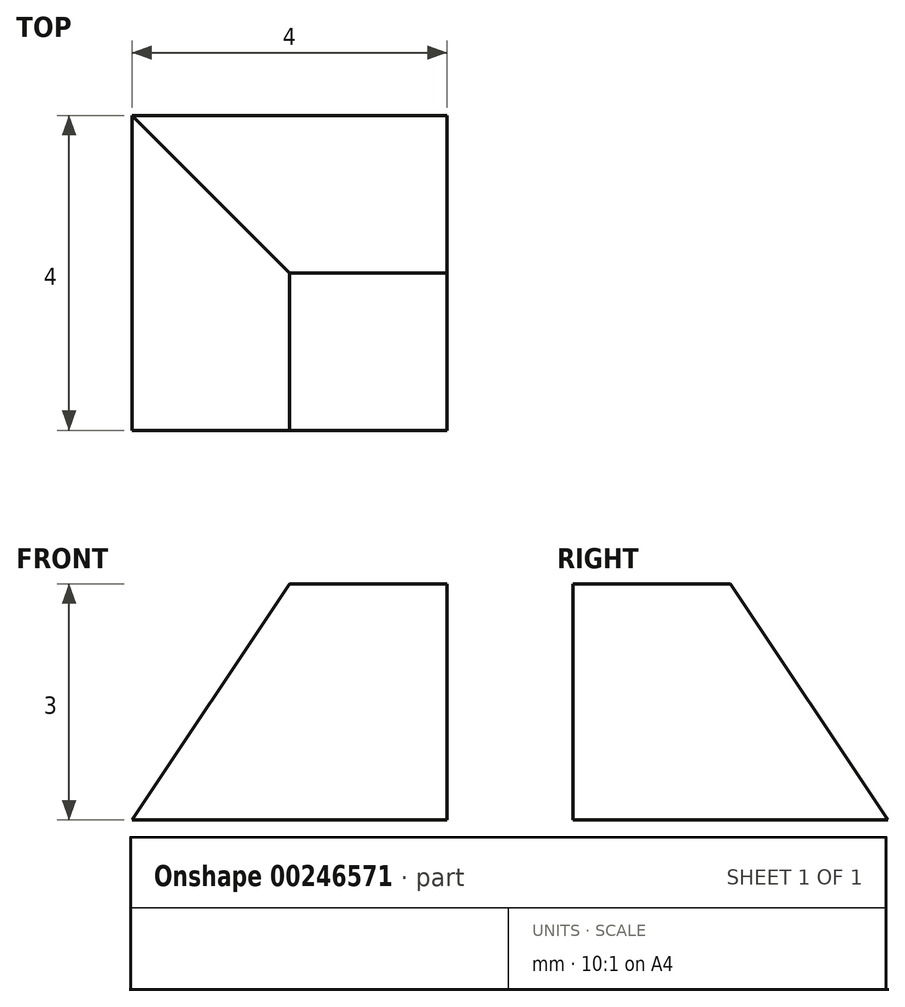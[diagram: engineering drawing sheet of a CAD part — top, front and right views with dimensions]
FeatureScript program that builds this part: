
annotation { "Feature Type Name" : "Feature", "Feature Type Description" : "" }
export const myFeature = defineFeature(function(context is Context, id is Id, definition is map)
    precondition{}
    {
        {
            var Q0;
            Q0=qCreatedBy(makeId("Top.planeOp"),FACE);
            var sketch = newSketch(context, id + "F0", { "sketchPlane" : qUnion([Q0])});
            skLineSegment(sketch, "E0.bottom", {"start": v(0, 0) * mm, "end": v(4, 0) * mm});
            skLineSegment(sketch, "E0.top", {"start": v(0, 4) * mm, "end": v(4, 4) * mm});
            skLineSegment(sketch, "E0.left", {"start": v(0, 0) * mm, "end": v(0, 4) * mm});
            skLineSegment(sketch, "E0.right", {"start": v(4, 0) * mm, "end": v(4, 4) * mm});
            skSolve(sketch);
        }
        {
            var Q0;
            Q0=makeQuery(id+"F0.imprint","IMPRINT",FACE,{"disambiguationData":[TD([[makeQuery(id+"F0.imprint","IMPRINT",EDGE,{"derivedFrom":sQuery(id+"F0.wireOp",EDGE,"E0.bottom")}),1.0]])]});
            extrude(context, id + "F1", {"entities" : qUnion([Q0]), "depth" : 3 * mm});
        }
        {
            var Q0;
            Q0=makeQuery(id+"F1.opExtrude","SWEPT_FACE",FACE,{"disambiguationData":[OSD([sQuery(id+"F0.wireOp",EDGE,"E0.right")])]});
            var sketch = newSketch(context, id + "F2", { "sketchPlane" : qUnion([Q0])});
            skLineSegment(sketch, "E1", {"start": v(4, 0) * mm, "end": v(2, 3) * mm});
            skLineSegment(sketch, "E2", {"start": v(0, 3) * mm, "end": v(2, 3) * mm});
            skSolve(sketch);
        }
        {
            var Q0;
            {var subQ0=sQuery(id+"F2.wireOp",EDGE,"E1");Q0=makeQuery(id+"F2.imprint","IMPRINT",FACE,{"disambiguationData":[TD([[makeQuery(id+"F2.imprint","IMPRINT",EDGE,{"derivedFrom":subQ0}),-1.0]])]});}
            extrude(context, id + "F3", {"entities" : qUnion([Q0]), "operationType" : NewBodyOperationType.REMOVE, "oppositeDirection" : true, "depth" : 25 * mm});
        }
        {
            var Q0;
            Q0=makeQuery(id+"F1.opExtrude","SWEPT_FACE",FACE,{"disambiguationData":[OSD([sQuery(id+"F0.wireOp",EDGE,"E0.bottom")])]});
            var sketch = newSketch(context, id + "F4", { "sketchPlane" : qUnion([Q0])});
            skLineSegment(sketch, "E3", {"start": v(4, 3) * mm, "end": v(2, 3) * mm});
            skLineSegment(sketch, "E4", {"start": v(2, 3) * mm, "end": v(0, 0) * mm});
            skSolve(sketch);
        }
        {
            var Q0;
            {var subQ0=sQuery(id+"F4.wireOp",EDGE,"E4");Q0=makeQuery(id+"F4.imprint","IMPRINT",FACE,{"disambiguationData":[TD([[makeQuery(id+"F4.imprint","IMPRINT",EDGE,{"derivedFrom":subQ0}),-1.0]])]});}
            extrude(context, id + "F5", {"entities" : qUnion([Q0]), "operationType" : NewBodyOperationType.REMOVE, "oppositeDirection" : true, "depth" : 25 * mm});
        }
    });
